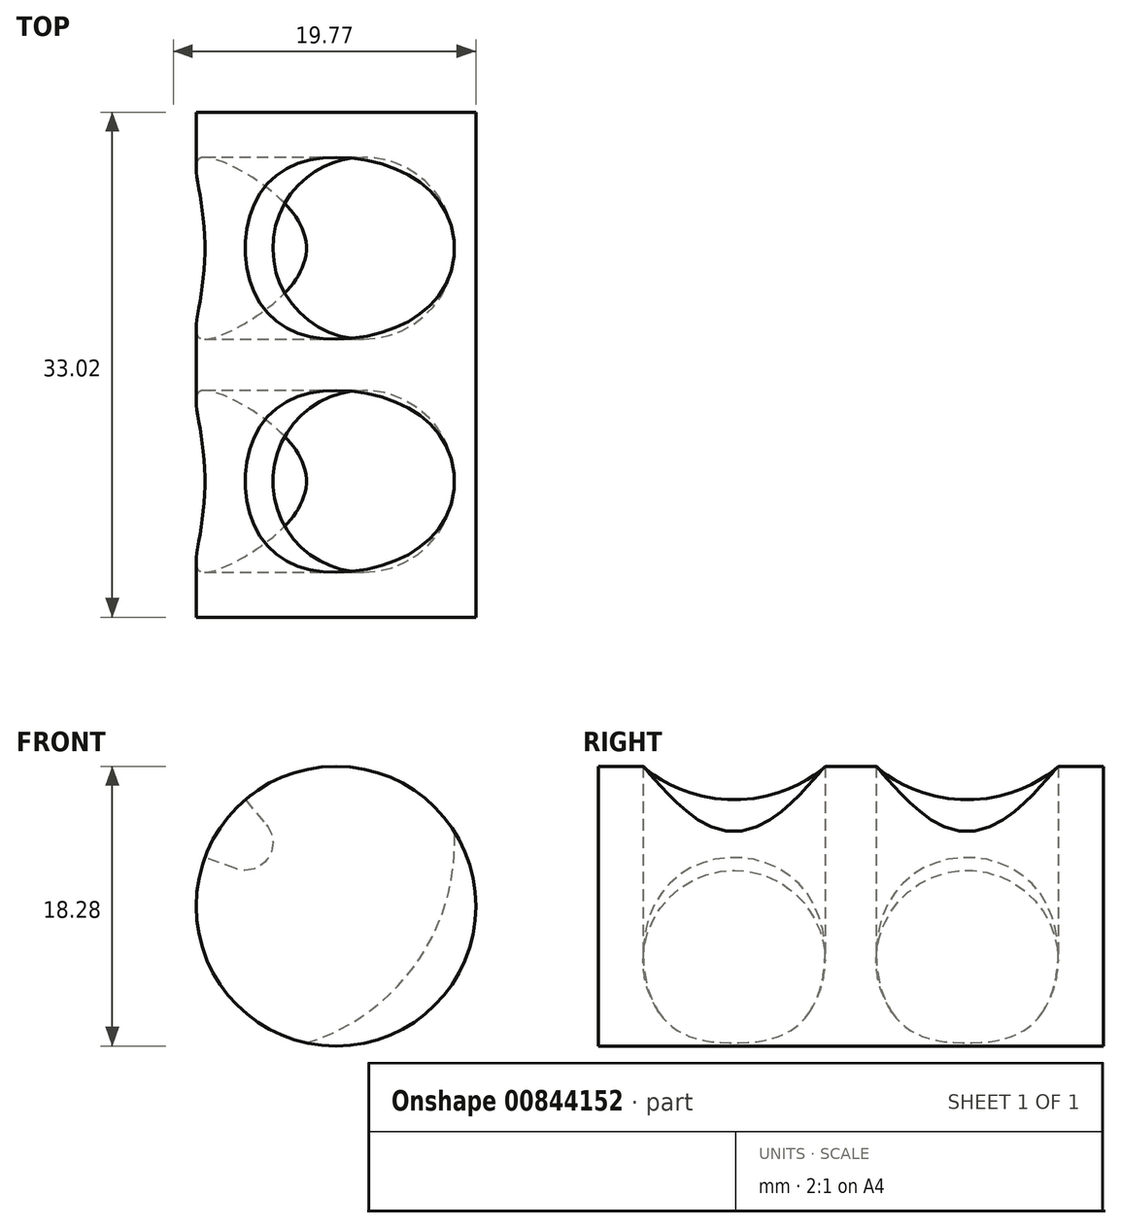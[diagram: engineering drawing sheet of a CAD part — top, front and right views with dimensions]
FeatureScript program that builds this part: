
annotation { "Feature Type Name" : "Feature", "Feature Type Description" : "" }
export const myFeature = defineFeature(function(context is Context, id is Id, definition is map)
    precondition{}
    {
        {
            var Q0;
            Q0=qCreatedBy(makeId("Front.planeOp"),FACE);
            var sketch = newSketch(context, id + "F0", { "sketchPlane" : qUnion([Q0])});
            skCircle(sketch, "E0", {"center": v(0, 0) * mm, "radius": 9.14 * mm});
            skLineSegment(sketch, "E1", {"start": v(-17.19, 0) * mm, "end": v(-8.6, -3.13) * mm});
            skLineSegment(sketch, "E2", {"start": v(0, 9.14) * mm, "end": v(-12.16, 23.63) * mm});
            skArc(sketch, "E3", {"start": v(-8.6, -3.13) * mm, "mid": v(0.41, -0.29) * mm, "end": v(0, 9.14) * mm});
            skLineSegment(sketch, "E4", {"start": v(0, 9.14) * mm, "end": v(0, 18.85) * mm});
            skLineSegment(sketch, "E5", {"start": v(0, 0) * mm, "end": v(-8.6, -3.13) * mm});
            skLineSegment(sketch, "E6", {"start": v(-8.6, -3.13) * mm, "end": v(-18.4, -6.7) * mm});
            skLineSegment(sketch, "E7", {"start": v(0, 9.14) * mm, "end": v(-8.6, -3.13) * mm});
            skLineSegment(sketch, "E8", {"start": v(-8.6, -3.13) * mm, "end": v(5.88, -7) * mm});
            skSolve(sketch);
        }
        {
            var Q0;
            {var subQ0=sQuery(id+"F0.wireOp",EDGE,"E3");Q0=makeQuery(id+"F0.imprint","IMPRINT",FACE,{"disambiguationData":[TD([[makeQuery(id+"F0.imprint","IMPRINT",EDGE,{"derivedFrom":subQ0}),1.0]])]});}
            var Q1;
            {var subQ0=sQuery(id+"F0.wireOp",EDGE,"E3");Q1=makeQuery(id+"F0.imprint","IMPRINT",FACE,{"disambiguationData":[TD([[makeQuery(id+"F0.imprint","IMPRINT",EDGE,{"derivedFrom":subQ0}),-1.0]])]});}
            var Q2;
            {var subQ0=sQuery(id+"F0.wireOp",EDGE,"E7");Q2=makeQuery(id+"F0.imprint","IMPRINT",FACE,{"disambiguationData":[TD([[makeQuery(id+"F0.imprint","IMPRINT",EDGE,{"derivedFrom":subQ0}),1.0]])]});}
            var Q3;
            {var subQ0=sQuery(id+"F0.wireOp",EDGE,"E7");Q3=makeQuery(id+"F0.imprint","IMPRINT",FACE,{"disambiguationData":[TD([[makeQuery(id+"F0.imprint","IMPRINT",EDGE,{"derivedFrom":subQ0}),-1.0]])]});}
            extrude(context, id + "F1", {"entities" : qUnion([Q0, Q1, Q2, Q3]), "depth" : 6.35 * mm, "offsetDistance" : 25.4 * mm, "hasSecondDirection" : true, "secondDirectionOppositeDirection" : true, "secondDirectionDepth" : 8.9 * mm});
        }
        {
            var Q0;
            Q0=sQuery(id+"F0.wireOp",EDGE,"E2");
            var Q1;
            Q1=sQuery(id+"F0.wireOp",VERTEX,"E2.end");
            cPlane(context, id + "F2", {"entities" : qUnion([Q0, Q1]), "cplaneType" : CPlaneType.LINE_POINT, "offset" : 25.4 * mm, "width" : 152.4 * mm, "height" : 152.4 * mm});
        }
        {
            var Q0;
            Q0=qCreatedBy(id+"F2.planeOp",FACE);
            var sketch = newSketch(context, id + "F3", { "sketchPlane" : qUnion([Q0])});
            skCircle(sketch, "E9", {"center": v(5.88, 0) * mm, "radius": 5.94 * mm});
            skSolve(sketch);
        }
        {
            var Q0;
            Q0=makeQuery(id+"F3.imprint","IMPRINT",FACE,{"disambiguationData":[TD([[makeQuery(id+"F3.imprint","IMPRINT",EDGE,{"derivedFrom":sQuery(id+"F3.wireOp",EDGE,"E9")}),1.0]])]});
            var Q1;
            Q1=sQuery(id+"F0.wireOp",EDGE,"E2");
            var Q2;
            Q2=sQuery(id+"F0.wireOp",EDGE,"E3");
            var Q3;
            Q3=sQuery(id+"F0.wireOp",EDGE,"E1");
            sweep(context, id + "F4", {"operationType" : NewBodyOperationType.REMOVE, "profiles" : qUnion([Q0]), "path" : qUnion([Q1, Q2, Q3])});
        }
        {
            var Q0;
            Q0=makeQuery(id+"F1.opExtrude","CAP_FACE",FACE,{"disambiguationData":[OSD([sQuery(id+"F0.wireOp",EDGE,"E0")])],"isStart":false});
            extrude(context, id + "F5", {"entities" : qUnion([Q0]), "operationType" : NewBodyOperationType.ADD, "depth" : 2.54 * mm, "offsetDistance" : 25.4 * mm});
        }
        {
            var Q0;
            Q0=makeQuery(id+"F5.opExtrude","CAP_FACE",FACE,{"disambiguationData":[OSD([sQuery(id+"F0.wireOp",EDGE,"E0")])],"isStart":false});
            extrude(context, id + "F6", {"entities" : qUnion([Q0]), "operationType" : NewBodyOperationType.ADD, "depth" : 15.24 * mm, "offsetDistance" : 25.4 * mm});
        }
        {
            var Q0;
            Q0=qCreatedBy(makeId("Front.planeOp"),FACE);
            cPlane(context, id + "F7", {"entities" : qUnion([Q0]), "cplaneType" : CPlaneType.OFFSET, "offset" : 15.24 * mm, "width" : 152.4 * mm, "height" : 152.4 * mm});
        }
        {
            var Q0;
            Q0=qCreatedBy(id+"F7.planeOp",FACE);
            var sketch = newSketch(context, id + "F8", { "sketchPlane" : qUnion([Q0])});
            skArc(sketch, "E10.0", {"start": v(-8.6, -3.13) * mm, "mid": v(0.41, -0.29) * mm, "end": v(0, 9.14) * mm});
            skLineSegment(sketch, "E11.0", {"start": v(-17.19, 0) * mm, "end": v(-8.6, -3.13) * mm});
            skLineSegment(sketch, "E12.0", {"start": v(0, 9.14) * mm, "end": v(-12.16, 23.63) * mm});
            skSolve(sketch);
        }
        {
            var Q0;
            Q0=qCreatedBy(id+"F2.planeOp",FACE);
            var sketch = newSketch(context, id + "F9", { "sketchPlane" : qUnion([Q0])});
            skCircle(sketch, "E13", {"center": v(5.88, -15.24) * mm, "radius": 5.94 * mm});
            skSolve(sketch);
        }
        {
            var Q0;
            Q0=makeQuery(id+"F9.imprint","IMPRINT",FACE,{"disambiguationData":[TD([[makeQuery(id+"F9.imprint","IMPRINT",EDGE,{"derivedFrom":sQuery(id+"F9.wireOp",EDGE,"E13")}),1.0]])]});
            var Q1;
            Q1=sQuery(id+"F8.wireOp",EDGE,"E12.0");
            var Q2;
            Q2=sQuery(id+"F8.wireOp",EDGE,"E10.0");
            var Q3;
            Q3=sQuery(id+"F8.wireOp",EDGE,"E11.0");
            sweep(context, id + "F10", {"operationType" : NewBodyOperationType.REMOVE, "profiles" : qUnion([Q0]), "path" : qUnion([Q1, Q2, Q3])});
        }
    });
